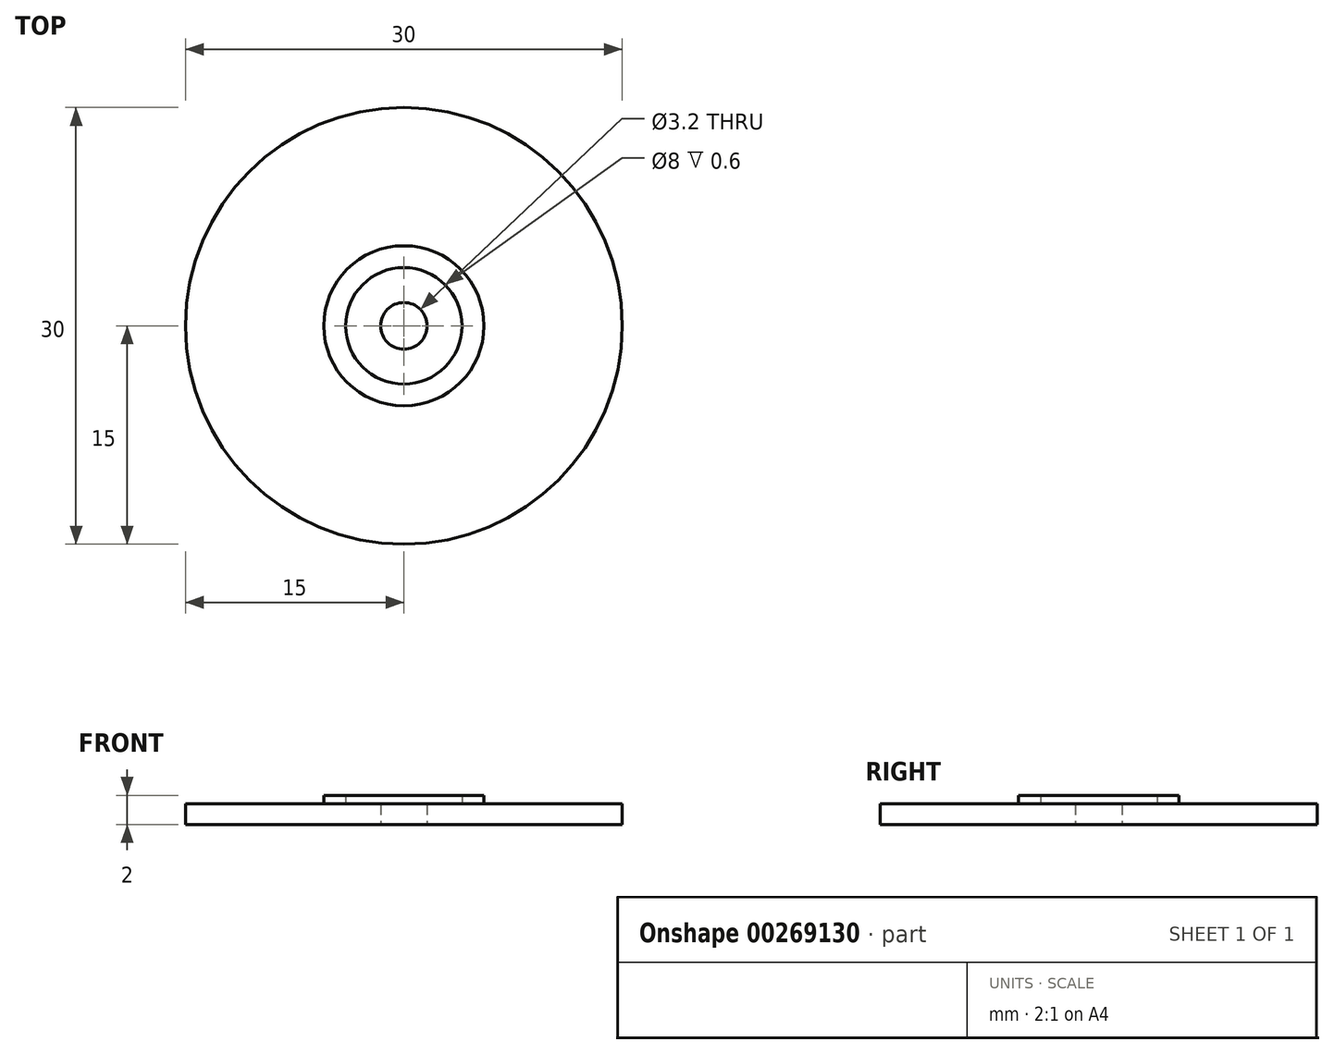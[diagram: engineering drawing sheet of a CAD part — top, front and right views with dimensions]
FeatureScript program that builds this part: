
annotation { "Feature Type Name" : "Feature", "Feature Type Description" : "" }
export const myFeature = defineFeature(function(context is Context, id is Id, definition is map)
    precondition{}
    {
        {
            var Q0;
            Q0=qCreatedBy(makeId("Top.planeOp"),FACE);
            var sketch = newSketch(context, id + "F0", { "sketchPlane" : qUnion([Q0])});
            skCircle(sketch, "E0", {"center": v(0, 0) * mm, "radius": 15 * mm});
            skCircle(sketch, "E1", {"center": v(0, 0) * mm, "radius": 1.6 * mm});
            skSolve(sketch);
        }
        {
            var Q0;
            Q0 = qSketchRegion(id + "F0", true);
            extrude(context, id + "F1", {"entities" : qUnion([Q0]), "depth" : 1.4 * mm});
        }
        {
            var Q0;
            Q0=makeQuery(id+"F1.opExtrude","CAP_FACE",FACE,{"disambiguationData":[OSD([sQuery(id+"F0.wireOp",EDGE,"E0"),sQuery(id+"F0.wireOp",EDGE,"E1")])],"isStart":false});
            var sketch = newSketch(context, id + "F2", { "sketchPlane" : qUnion([Q0])});
            skCircle(sketch, "E2", {"center": v(0, 0) * mm, "radius": 4 * mm});
            skCircle(sketch, "E3", {"center": v(0, 0) * mm, "radius": 5.5 * mm});
            skSolve(sketch);
        }
        {
            var Q0;
            Q0=makeQuery(id+"F2.imprint","IMPRINT",FACE,{"disambiguationData":[TD([[makeQuery(id+"F2.imprint","IMPRINT",EDGE,{"derivedFrom":sQuery(id+"F2.wireOp",EDGE,"E2")}),-1.0]])]});
            var Q1;
            Q1=makeQuery(id+"F2.imprint","IMPRINT",FACE,{"disambiguationData":[TD([[makeQuery(id+"F2.imprint","IMPRINT",EDGE,{"derivedFrom":sQuery(id+"F2.wireOp",EDGE,"31pFEaqM-Zwgb-LQ5u-HBD7-Mvmt9LJR8j5u")}),-1.0]])]});
            extrude(context, id + "F3", {"entities" : qUnion([Q0, Q1]), "operationType" : NewBodyOperationType.ADD, "depth" : .6 * mm});
        }
    });
